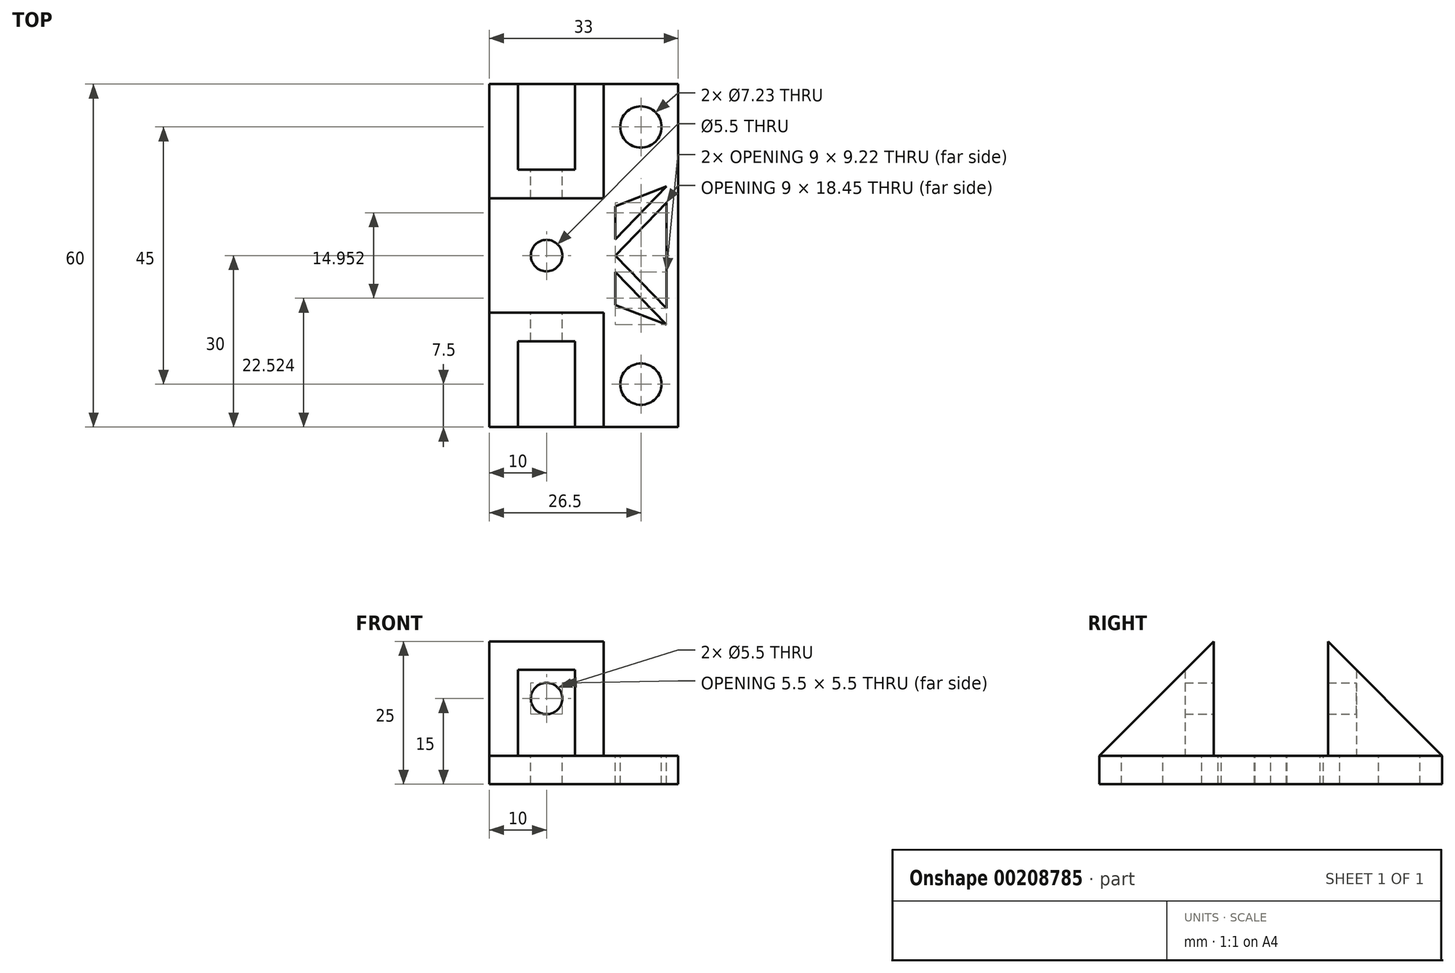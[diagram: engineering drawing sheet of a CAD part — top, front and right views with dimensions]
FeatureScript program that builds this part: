
annotation { "Feature Type Name" : "Feature", "Feature Type Description" : "" }
export const myFeature = defineFeature(function(context is Context, id is Id, definition is map)
    precondition{}
    {
        {
            var Q0;
            Q0=qCreatedBy(makeId("Top.planeOp"),FACE);
            var sketch = newSketch(context, id + "F0", { "sketchPlane" : qUnion([Q0])});
            skLineSegment(sketch, "E0", {"start": v(0, 0) * mm, "end": v(33, 0) * mm});
            skLineSegment(sketch, "E1", {"start": v(33, 0) * mm, "end": v(33, -15) * mm});
            skLineSegment(sketch, "E2", {"start": v(33, -15) * mm, "end": v(20, -20) * mm, "construction": true});
            skLineSegment(sketch, "E3", {"start": v(20, -20) * mm, "end": v(20, -40) * mm, "construction": true});
            skLineSegment(sketch, "E4", {"start": v(20, -40) * mm, "end": v(33, -45) * mm, "construction": true});
            skLineSegment(sketch, "E5", {"start": v(33, -45) * mm, "end": v(33, -60) * mm});
            skLineSegment(sketch, "E6", {"start": v(33, -60) * mm, "end": v(0, -60) * mm});
            skLineSegment(sketch, "E7", {"start": v(0, -60) * mm, "end": v(0, 0) * mm});
            skLineSegment(sketch, "E8", {"start": v(20, -30) * mm, "end": v(0, -30) * mm, "construction": true});
            skPoint(sketch, "E9", {"position": v(10, -30) * mm});
            skPoint(sketch, "E10", {"position": v(26.5, -7.5) * mm});
            skPoint(sketch, "E10.positionSnap0", {"position": v(26.5, -17.5) * mm});
            skPoint(sketch, "E10.positionSnap1", {"position": v(33, -7.5) * mm});
            skPoint(sketch, "E11", {"position": v(26.5, -52.5) * mm});
            skPoint(sketch, "E11.positionSnap0", {"position": v(33, -52.5) * mm});
            skPoint(sketch, "E11.positionSnap1", {"position": v(26.5, -42.5) * mm});
            skLineSegment(sketch, "E12", {"start": v(33, -45) * mm, "end": v(33, -15) * mm});
            skSolve(sketch);
        }
        {
            var Q0;
            Q0=makeQuery(id+"F0.imprint","IMPRINT",FACE,{"disambiguationData":[TD([[makeQuery(id+"F0.imprint","IMPRINT",EDGE,{"derivedFrom":sQuery(id+"F0.wireOp",EDGE,"E0")}),-1.0]])]});
            extrude(context, id + "F1", {"entities" : qUnion([Q0]), "depth" : 5 * mm});
        }
        {
            var Q0;
            Q0=makeQuery(id+"F1.opExtrude","CAP_FACE",FACE,{"disambiguationData":[OSD([sQuery(id+"F0.wireOp",EDGE,"E0"),sQuery(id+"F0.wireOp",EDGE,"E1"),sQuery(id+"F0.wireOp",EDGE,"E2"),sQuery(id+"F0.wireOp",EDGE,"E3"),sQuery(id+"F0.wireOp",EDGE,"E4"),sQuery(id+"F0.wireOp",EDGE,"E5"),sQuery(id+"F0.wireOp",EDGE,"E6"),sQuery(id+"F0.wireOp",EDGE,"E7")])],"isStart":false});
            var sketch = newSketch(context, id + "F2", { "sketchPlane" : qUnion([Q0])});
            skLineSegment(sketch, "E13", {"start": v(20, -20) * mm, "end": v(20, 0) * mm});
            skLineSegment(sketch, "E14", {"start": v(20, 0) * mm, "end": v(15, 0) * mm});
            skLineSegment(sketch, "E15", {"start": v(15, 0) * mm, "end": v(15, -15) * mm});
            skLineSegment(sketch, "E16", {"start": v(15, -15) * mm, "end": v(5, -15) * mm});
            skLineSegment(sketch, "E17", {"start": v(5, -15) * mm, "end": v(5, 0) * mm});
            skLineSegment(sketch, "E18", {"start": v(5, 0) * mm, "end": v(0, 0) * mm});
            skLineSegment(sketch, "E19", {"start": v(0, 0) * mm, "end": v(0, -20) * mm});
            skLineSegment(sketch, "E20", {"start": v(0, -20) * mm, "end": v(20, -20) * mm});
            skLineSegment(sketch, "E21", {"start": v(20, -40) * mm, "end": v(0, -40) * mm});
            skLineSegment(sketch, "E22", {"start": v(0, -40) * mm, "end": v(0, -60) * mm});
            skLineSegment(sketch, "E23", {"start": v(0, -60) * mm, "end": v(5, -60) * mm});
            skLineSegment(sketch, "E24", {"start": v(5, -60) * mm, "end": v(5, -45) * mm});
            skLineSegment(sketch, "E25", {"start": v(5, -45) * mm, "end": v(15, -45) * mm});
            skLineSegment(sketch, "E26", {"start": v(15, -45) * mm, "end": v(15, -60) * mm});
            skLineSegment(sketch, "E27", {"start": v(15, -60) * mm, "end": v(20, -60) * mm});
            skLineSegment(sketch, "E28", {"start": v(20, -60) * mm, "end": v(20, -40) * mm});
            skSolve(sketch);
        }
        {
            var Q0;
            Q0=makeQuery(id+"F2.imprint","IMPRINT",FACE,{"disambiguationData":[TD([[makeQuery(id+"F2.imprint","IMPRINT",EDGE,{"derivedFrom":sQuery(id+"F2.wireOp",EDGE,"E13")}),1.0]])]});
            var Q1;
            Q1=makeQuery(id+"F2.imprint","IMPRINT",FACE,{"disambiguationData":[TD([[makeQuery(id+"F2.imprint","IMPRINT",EDGE,{"derivedFrom":sQuery(id+"F2.wireOp",EDGE,"E21")}),1.0]])]});
            extrude(context, id + "F3", {"entities" : qUnion([Q0, Q1]), "operationType" : NewBodyOperationType.ADD, "depth" : 20 * mm});
        }
        {
            var Q0;
            Q0=makeQuery(id+"F3.opExtrude","SWEPT_FACE",FACE,{"disambiguationData":[OSD([sQuery(id+"F2.wireOp",EDGE,"E28")])]});
            var sketch = newSketch(context, id + "F4", { "sketchPlane" : qUnion([Q0])});
            skLineSegment(sketch, "E29", {"start": v(-40, 25) * mm, "end": v(-60, 5) * mm});
            skLineSegment(sketch, "E30", {"start": v(-60, 5) * mm, "end": v(-60, 25) * mm});
            skLineSegment(sketch, "E31", {"start": v(-60, 25) * mm, "end": v(-40, 25) * mm});
            skLineSegment(sketch, "E32", {"start": v(-20, 25) * mm, "end": v(0, 25) * mm});
            skLineSegment(sketch, "E33", {"start": v(0, 25) * mm, "end": v(0, 5) * mm});
            skLineSegment(sketch, "E34", {"start": v(0, 5) * mm, "end": v(-20, 25) * mm});
            skSolve(sketch);
        }
        {
            var Q0;
            Q0=makeQuery(id+"F4.imprint","IMPRINT",FACE,{"disambiguationData":[TD([[makeQuery(id+"F4.imprint","IMPRINT",EDGE,{"derivedFrom":sQuery(id+"F4.wireOp",EDGE,"E32")}),-1.0]])]});
            var Q1;
            Q1=makeQuery(id+"F4.imprint","IMPRINT",FACE,{"disambiguationData":[TD([[makeQuery(id+"F4.imprint","IMPRINT",EDGE,{"derivedFrom":sQuery(id+"F4.wireOp",EDGE,"E29")}),-1.0]])]});
            extrude(context, id + "F5", {"entities" : qUnion([Q0, Q1]), "operationType" : NewBodyOperationType.REMOVE, "endBound" : BoundingType.THROUGH_ALL, "oppositeDirection" : true, "depth" : 25 * mm});
        }
        {
            var Q0;
            Q0=makeQuery(id+"F3.opExtrude","SWEPT_FACE",FACE,{"disambiguationData":[OSD([sQuery(id+"F2.wireOp",EDGE,"E25")])]});
            var sketch = newSketch(context, id + "F6", { "sketchPlane" : qUnion([Q0])});
            skLineSegment(sketch, "E35", {"start": v(10, 5) * mm, "end": v(10, 25) * mm});
            skPoint(sketch, "E36", {"position": v(10, 15) * mm});
            skSolve(sketch);
        }
        {
            var Q0;
            Q0=sQuery(id+"F0.wireOp",VERTEX,"E10");
            var Q1;
            Q1=sQuery(id+"F0.wireOp",VERTEX,"E11");
            var Q2;
            Q2=makeQuery(id+"F1.opExtrude","SWEPT_BODY",BODY,{"disambiguationData":[OSD([sQuery(id+"F0.wireOp",EDGE,"E0"),sQuery(id+"F0.wireOp",EDGE,"E1"),sQuery(id+"F0.wireOp",EDGE,"E2"),sQuery(id+"F0.wireOp",EDGE,"E3"),sQuery(id+"F0.wireOp",EDGE,"E4"),sQuery(id+"F0.wireOp",EDGE,"E5"),sQuery(id+"F0.wireOp",EDGE,"E6"),sQuery(id+"F0.wireOp",EDGE,"E7")])]});
            hole(context, id + "F7", {"style" : HoleStyle.SIMPLE, "endStyle" : HoleEndStyle.THROUGH, "oppositeDirection" : true, "holeDiameter" : 7.23 * mm, "locations" : qUnion([Q0, Q1]), "scope" : qUnion([Q2]), "isTappedThrough" : true});
        }
        {
            var Q0;
            {var subQ0=sQuery(id+"F0.wireOp",EDGE,"E0");var subQ1=sQuery(id+"F0.wireOp",EDGE,"E12");var subQ2=sQuery(id+"F0.wireOp",EDGE,"E5");var subQ3=sQuery(id+"F0.wireOp",EDGE,"E1");var subQ4=sQuery(id+"F0.wireOp",EDGE,"E6");var subQ5=sQuery(id+"F0.wireOp",EDGE,"E7");Q0=makeQuery(id+"F3.boolean.opBoolean","SPLIT",FACE,{"disambiguationData":[TD([makeQuery(id+"F1.opExtrude","SWEPT_FACE",FACE,{"disambiguationData":[OSD([subQ5])]})])],"derivedFrom":makeQuery(id+"F1.opExtrude","CAP_FACE",FACE,{"disambiguationData":[OSD([subQ0,subQ3,subQ2,subQ4,subQ5,subQ1])],"isStart":false})});}
            var sketch = newSketch(context, id + "F8", { "sketchPlane" : qUnion([Q0])});
            skLineSegment(sketch, "E37", {"start": v(31, -17.91) * mm, "end": v(22, -21.37) * mm});
            skLineSegment(sketch, "E38", {"start": v(22, -38.63) * mm, "end": v(31, -42.09) * mm});
            skLineSegment(sketch, "E39", {"start": v(22, -38.63) * mm, "end": v(22, -32.86) * mm});
            skLineSegment(sketch, "E40", {"start": v(22, -32.86) * mm, "end": v(31, -42.09) * mm});
            skLineSegment(sketch, "E41", {"start": v(22, -21.37) * mm, "end": v(22, -27.14) * mm});
            skLineSegment(sketch, "E42", {"start": v(31, -20.78) * mm, "end": v(22, -30) * mm});
            skLineSegment(sketch, "E43", {"start": v(22, -30) * mm, "end": v(31, -39.22) * mm});
            skLineSegment(sketch, "E44", {"start": v(31, -39.22) * mm, "end": v(31, -20.78) * mm});
            skLineSegment(sketch, "E45", {"start": v(22, -27.14) * mm, "end": v(31, -17.91) * mm});
            skLineSegment(sketch, "E46", {"start": v(31, -30) * mm, "end": v(22, -30) * mm, "construction": true});
            skSolve(sketch);
        }
        {
            var Q0;
            Q0=makeQuery(id+"F8.imprint","IMPRINT",FACE,{"disambiguationData":[TD([[makeQuery(id+"F8.imprint","IMPRINT",EDGE,{"derivedFrom":sQuery(id+"F8.wireOp",EDGE,"E42")}),1.0]])]});
            var Q1;
            Q1=makeQuery(id+"F8.imprint","IMPRINT",FACE,{"disambiguationData":[TD([[makeQuery(id+"F8.imprint","IMPRINT",EDGE,{"derivedFrom":sQuery(id+"F8.wireOp",EDGE,"E37")}),1.0]])]});
            var Q2;
            Q2=makeQuery(id+"F8.imprint","IMPRINT",FACE,{"disambiguationData":[TD([[makeQuery(id+"F8.imprint","IMPRINT",EDGE,{"derivedFrom":sQuery(id+"F8.wireOp",EDGE,"E38")}),1.0]])]});
            var Q3;
            Q3=sQuery(id+"F8.wireOp",EDGE,"E46");
            extrude(context, id + "F9", {"entities" : qUnion([Q0, Q1, Q2]), "operationType" : NewBodyOperationType.REMOVE, "surfaceEntities" : qUnion([Q3]), "endBound" : BoundingType.THROUGH_ALL, "oppositeDirection" : true, "depth" : 25 * mm});
        }
        {
            var Q0;
            Q0=sQuery(id+"F0.wireOp",VERTEX,"E9");
            var Q1;
            Q1=makeQuery(id+"F1.opExtrude","SWEPT_BODY",BODY,{"disambiguationData":[OSD([sQuery(id+"F0.wireOp",EDGE,"E0"),sQuery(id+"F0.wireOp",EDGE,"E1"),sQuery(id+"F0.wireOp",EDGE,"E2"),sQuery(id+"F0.wireOp",EDGE,"E3"),sQuery(id+"F0.wireOp",EDGE,"E4"),sQuery(id+"F0.wireOp",EDGE,"E5"),sQuery(id+"F0.wireOp",EDGE,"E6"),sQuery(id+"F0.wireOp",EDGE,"E7")])]});
            hole(context, id + "F10", {"style" : HoleStyle.SIMPLE, "endStyle" : HoleEndStyle.THROUGH, "oppositeDirection" : true, "standardTappedOrClearance" : lookupTablePath({ "standard" : "ISO", "fit" : "Normal", "size" : "M5", "type" : "Clearance" }), "standardBlindInLast" : lookupTablePath({ "fit" : "Standard", "standard" : "ISO", "size" : "M5", "type" : "Clearance" }), "holeDiameter" : 5.5 * mm, "locations" : qUnion([Q0]), "scope" : qUnion([Q1]), "isTappedThrough" : true});
        }
        {
            var Q0;
            Q0=sQuery(id+"F6.wireOp",VERTEX,"E36");
            var Q1;
            Q1=makeQuery(id+"F1.opExtrude","SWEPT_BODY",BODY,{"disambiguationData":[OSD([sQuery(id+"F0.wireOp",EDGE,"E0"),sQuery(id+"F0.wireOp",EDGE,"E1"),sQuery(id+"F0.wireOp",EDGE,"E2"),sQuery(id+"F0.wireOp",EDGE,"E3"),sQuery(id+"F0.wireOp",EDGE,"E4"),sQuery(id+"F0.wireOp",EDGE,"E5"),sQuery(id+"F0.wireOp",EDGE,"E6"),sQuery(id+"F0.wireOp",EDGE,"E7")])]});
            hole(context, id + "F11", {"style" : HoleStyle.SIMPLE, "endStyle" : HoleEndStyle.THROUGH, "standardTappedOrClearance" : lookupTablePath({ "standard" : "ISO", "fit" : "Normal", "size" : "M5", "type" : "Clearance" }), "standardBlindInLast" : lookupTablePath({ "fit" : "Standard", "standard" : "ISO", "size" : "M5", "type" : "Clearance" }), "holeDiameter" : 5.5 * mm, "locations" : qUnion([Q0]), "scope" : qUnion([Q1]), "isTappedThrough" : true});
        }
    });
